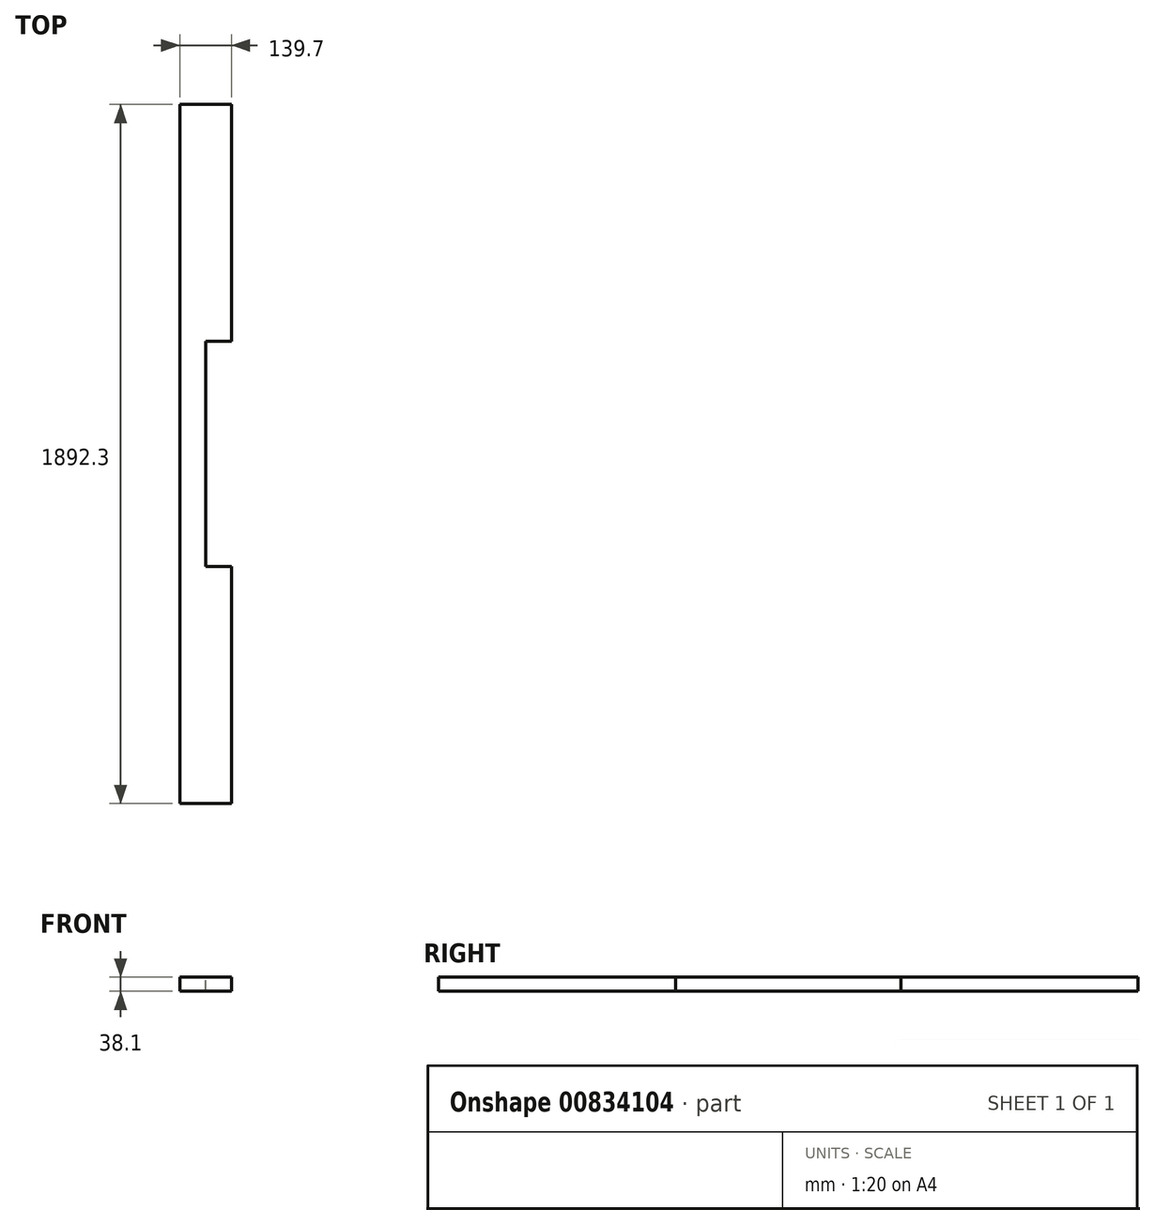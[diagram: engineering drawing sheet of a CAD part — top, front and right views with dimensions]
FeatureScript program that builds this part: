
annotation { "Feature Type Name" : "Feature", "Feature Type Description" : "" }
export const myFeature = defineFeature(function(context is Context, id is Id, definition is map)
    precondition{}
    {
        {
            var Q0;
            Q0=qCreatedBy(makeId("Front.planeOp"),FACE);
            var sketch = newSketch(context, id + "F0", { "sketchPlane" : qUnion([Q0])});
            skLineSegment(sketch, "E0.bottom", {"start": v(69.85, -19.05) * mm, "end": v(-69.85, -19.05) * mm});
            skLineSegment(sketch, "E0.top", {"start": v(69.85, 19.05) * mm, "end": v(-69.85, 19.05) * mm});
            skLineSegment(sketch, "E0.left", {"start": v(69.85, -19.05) * mm, "end": v(69.85, 19.05) * mm});
            skLineSegment(sketch, "E0.right", {"start": v(-69.85, -19.05) * mm, "end": v(-69.85, 19.05) * mm});
            skPoint(sketch, "E0.middle", {"position": v(0, 0) * mm});
            skSolve(sketch);
        }
        {
            var Q0;
            Q0=qSketchRegion(id+"F0",true);
            extrude(context, id + "F1", {"entities" : qUnion([Q0]), "endBound" : BoundingType.SYMMETRIC, "depth" : 1892.3 * mm});
        }
        {
            var Q0;
            Q0=makeQuery(id+"F1.opExtrude","SWEPT_FACE",FACE,{"disambiguationData":[OSD([sQuery(id+"F0.wireOp",EDGE,"E0.top")])]});
            var sketch = newSketch(context, id + "F2", { "sketchPlane" : qUnion([Q0])});
            skLineSegment(sketch, "E1.bottom", {"start": v(0, -304.8) * mm, "end": v(139.7, -304.8) * mm});
            skLineSegment(sketch, "E1.top", {"start": v(0, 304.8) * mm, "end": v(139.7, 304.8) * mm});
            skLineSegment(sketch, "E1.left", {"start": v(0, -304.8) * mm, "end": v(0, 304.8) * mm});
            skLineSegment(sketch, "E1.right", {"start": v(139.7, -304.8) * mm, "end": v(139.7, 304.8) * mm});
            skPoint(sketch, "E1.middle", {"position": v(69.85, 0) * mm});
            skSolve(sketch);
        }
        {
            var Q0;
            Q0=qSketchRegion(id+"F2",true);
            extrude(context, id + "F3", {"entities" : qUnion([Q0]), "operationType" : NewBodyOperationType.REMOVE, "endBound" : BoundingType.THROUGH_ALL, "oppositeDirection" : true, "depth" : 25.4 * mm});
        }
    });
